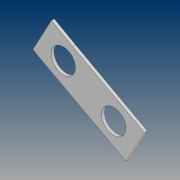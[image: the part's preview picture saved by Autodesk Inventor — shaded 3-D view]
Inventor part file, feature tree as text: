
AUTODESK INVENTOR PART (.ipt)
format: ipt  version: 2021 (Build 250183000, 183)  size: 102,912 bytes
history: native  units: mm
features: extrude x1
ambient origin geometry x8: Origin, YZ Plane, XZ Plane, XY Plane, X Axis, Y Axis, Z Axis, Center Point
bodies: Solid1 (feature_tree)
feature tree (1):
  extrude  "Extrusion1"  Depth=3.0mm TaperAngle=0.0deg
